# Revit family: WIR-RMI
name_source: partatom
category: Communication Devices
units: mm (PartAtom-declared; Revit-internal decimal feet)

## family parameters
Cut with Voids When Loaded = No
Host = Face
Maintain Annotation Orientation = No
OmniClass Number = 23.85.80.11.27
OmniClass Title = Lighting Controls
Part Type = Normal
Room Calculation Point = No
Round Connector Dimension = Use Diameter
Shared = Yes

## types (1)
- WIR-RMI
    Assembly Code = D5090
    Black Element = Metal-Nickel
    Blue Element = Metal-Aluminum Anodized Blue
    Certification = UL: E485483
2.4GHz Version - FCC: U.S. FCC Part 15.247 Class A: OUR-XBEE / OUR-XBEE PRO, Canada IC: 4214A-XBEE /
4214A-XBEE PRO, Europe CE: ETSI / ETSI
900MHz Version - FCC: U.S. FCC Part 15.247 Class A: MCQ-XB900HP
UL94V-0 Flame retardant ABS or epoxy molding
    Default Elevation = 48 "
    Description = The wiSCAPE® Wireless Internal Fixture Module is a bidirectional wireless RF device that allows an individual fixture to be managed, monitored and metered. The wiSCAPE Module can switch loads of up to 7 Amps @ 120V to 347V or 2 Amps @ 480V. Universal input voltage allows the module to function on 120-480V circuits at 50/60 Hz. The Fixture Module works with all fixture types including: LED, Induction, MH-HPS-LPS, Incandescent, Halogen andPlasma. The adaptable sink and source 0-10V output is compatible with all dimming drivers. Digital and analog inputs and outputs make sending and receiving signals from additional control devices simple and easy.
    Features = 3 Digital inputs / 1 analog input for low-voltage switch, motion
and photo sensors
• Universal dimmer 1-10V (sink/source) for all types of ballasts & drivers
• 2 Dry contact outputs for driving external contactors
• Bidirectional long range wireless RF Mesh communications
• Integration with wiSCAPE software
• Multi-level grouping and multiple scenarios
• Adjustable minimum and maximum dimming levels
• Programmable state after blackout, with peak shaving options
• Commercial-grade metering
• Smart daylight harvesting and motion sensing functions, with occupied
and unoccupied levels including a lamp saver function
• Manual-ON/Auto-OFF, Auto-ON/Auto-OFF and grace period compliant
(complies with N.Y. LL48 and many other energy requirements
and incentives)
    Green = Paint - Green
    Housing Material = Paint -  Matte White
    Length = 4.75 "
    Manufacturer = NX Lighting Controls
    Model = WIR-RMI
    Type Comments = wiSCAPE® Internal Fixture Module
    URL = https://www.currentlighting.com
    Warranty = 5-Years Warranty
    Width = 2.65 "

## geometry (parser evidence)
native form markers: Sweep x2
no freeform markers — native parametric forms only
